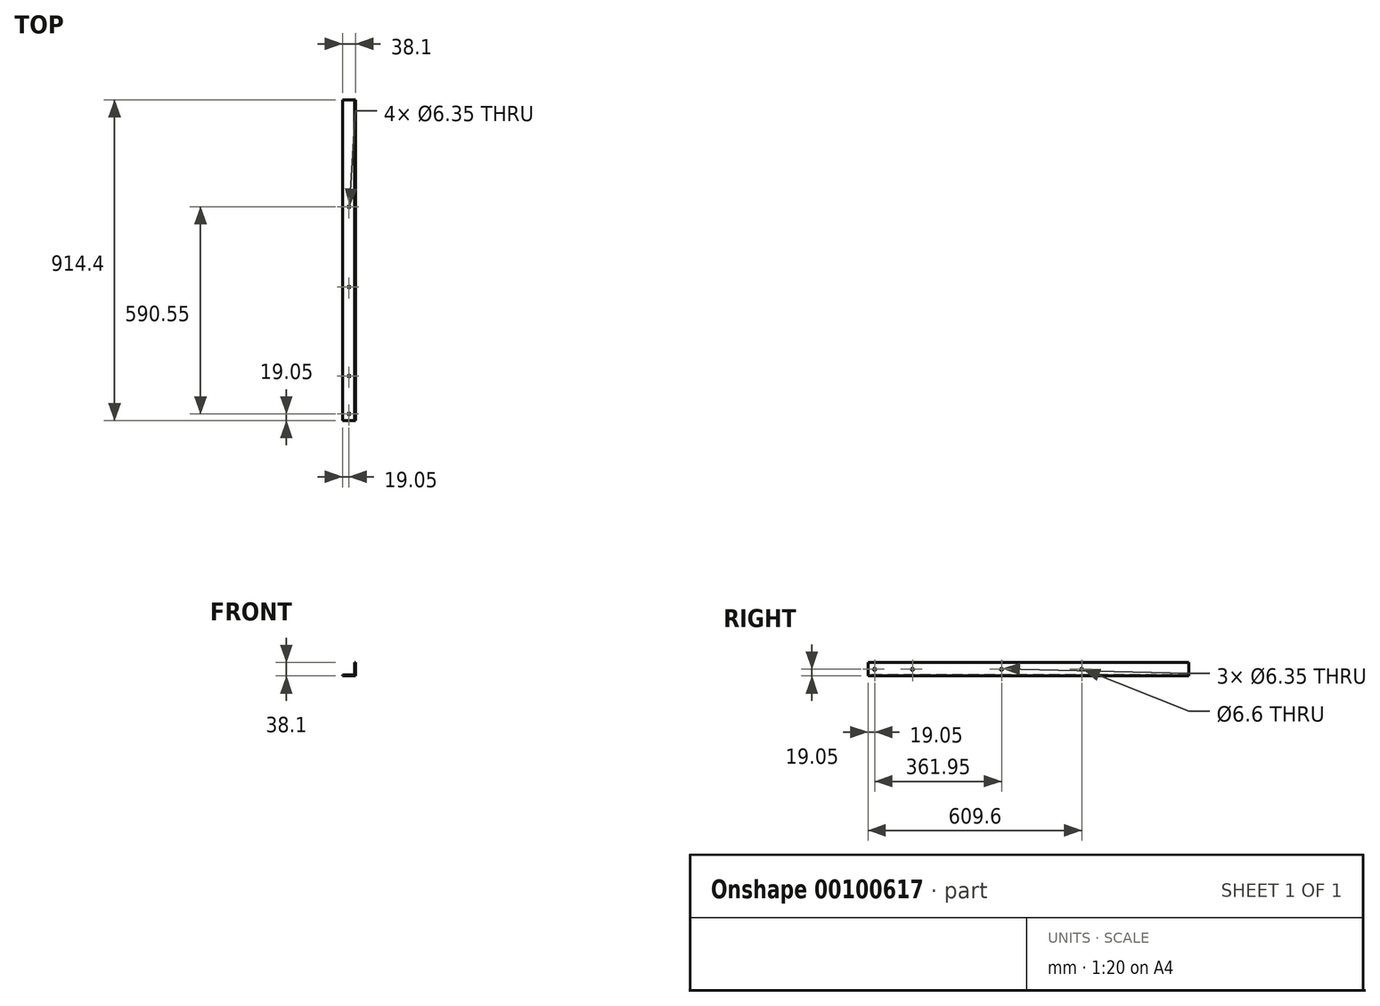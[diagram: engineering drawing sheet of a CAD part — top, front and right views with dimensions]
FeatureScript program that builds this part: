
annotation { "Feature Type Name" : "Feature", "Feature Type Description" : "" }
export const myFeature = defineFeature(function(context is Context, id is Id, definition is map)
    precondition{}
    {
        {
            var Q0;
            Q0=qCreatedBy(makeId("Front.planeOp"),FACE);
            var sketch = newSketch(context, id + "F0", { "sketchPlane" : qUnion([Q0])});
            skLineSegment(sketch, "E0", {"start": v(-19.05, -19.05) * mm, "end": v(19.05, -19.05) * mm});
            skLineSegment(sketch, "E1", {"start": v(19.05, -19.05) * mm, "end": v(19.05, 19.05) * mm});
            skPoint(sketch, "E2", {"position": v(0, -19.05) * mm});
            skLineSegment(sketch, "E3", {"start": v(15.87, 19.05) * mm, "end": v(19.05, 19.05) * mm});
            skPoint(sketch, "E4", {"position": v(19.05, 0) * mm});
            skLineSegment(sketch, "E5.0", {"start": v(15.87, -15.88) * mm, "end": v(15.87, 19.05) * mm});
            skLineSegment(sketch, "E5.1", {"start": v(-19.05, -15.88) * mm, "end": v(15.87, -15.88) * mm});
            skLineSegment(sketch, "E6", {"start": v(-19.05, -19.05) * mm, "end": v(-19.05, -15.88) * mm});
            skSolve(sketch);
        }
        {
            var Q0;
            Q0 = qSketchRegion(id + "F0", true);
            extrude(context, id + "F1", {"entities" : qUnion([Q0]), "oppositeDirection" : true, "depth" : 203.2 * mm});
        }
        {
            var Q0;
            Q0 = qSketchRegion(id + "F0", true);
            extrude(context, id + "F2", {"entities" : qUnion([Q0]), "operationType" : NewBodyOperationType.ADD, "oppositeDirection" : true, "depth" : 914.4 * mm});
        }
        {
            var Q0;
            {var subQ0=sQuery(id+"F0.wireOp",EDGE,"E5.0");Q0=makeQuery(id+"F2.boolean.opBoolean","MERGE",FACE,{"derivedFrom":[makeQuery(id+"F1.opExtrude","SWEPT_FACE",FACE,{"disambiguationData":[OSD([subQ0])]}),makeQuery(id+"F2.opExtrude","SWEPT_FACE",FACE,{"disambiguationData":[OSD([subQ0])]})]});}
            var sketch = newSketch(context, id + "F3", { "sketchPlane" : qUnion([Q0])});
            skCircle(sketch, "E7", {"center": v(-609.6, 0) * mm, "radius": 3.3 * mm});
            skCircle(sketch, "E8", {"center": v(-19.05, 0) * mm, "radius": 3.18 * mm});
            skCircle(sketch, "E9", {"center": v(-127, 0) * mm, "radius": 3.18 * mm});
            skCircle(sketch, "E10", {"center": v(-381, 0) * mm, "radius": 3.17 * mm});
            skSolve(sketch);
        }
        {
            var Q0;
            Q0 = qSketchRegion(id + "F3", true);
            extrude(context, id + "F4", {"entities" : qUnion([Q0]), "operationType" : NewBodyOperationType.REMOVE, "oppositeDirection" : true, "depth" : 32.7 * mm});
        }
        {
            var Q0;
            {var subQ0=sQuery(id+"F0.wireOp",EDGE,"E0");Q0=makeQuery(id+"F2.boolean.opBoolean","MERGE",FACE,{"derivedFrom":[makeQuery(id+"F1.opExtrude","SWEPT_FACE",FACE,{"disambiguationData":[OSD([subQ0])]}),makeQuery(id+"F2.opExtrude","SWEPT_FACE",FACE,{"disambiguationData":[OSD([subQ0])]})]});}
            var sketch = newSketch(context, id + "F5", { "sketchPlane" : qUnion([Q0])});
            skCircle(sketch, "E11", {"center": v(0, -609.6) * mm, "radius": 3.18 * mm});
            skCircle(sketch, "E12", {"center": v(0, -19.05) * mm, "radius": 3.18 * mm});
            skCircle(sketch, "E13", {"center": v(0, -127) * mm, "radius": 3.18 * mm});
            skCircle(sketch, "E14", {"center": v(0, -381) * mm, "radius": 3.18 * mm});
            skSolve(sketch);
        }
        {
            var Q0;
            Q0 = qSketchRegion(id + "F5", true);
            extrude(context, id + "F6", {"entities" : qUnion([Q0]), "operationType" : NewBodyOperationType.REMOVE, "oppositeDirection" : true, "depth" : 25.4 * mm});
        }
    });
